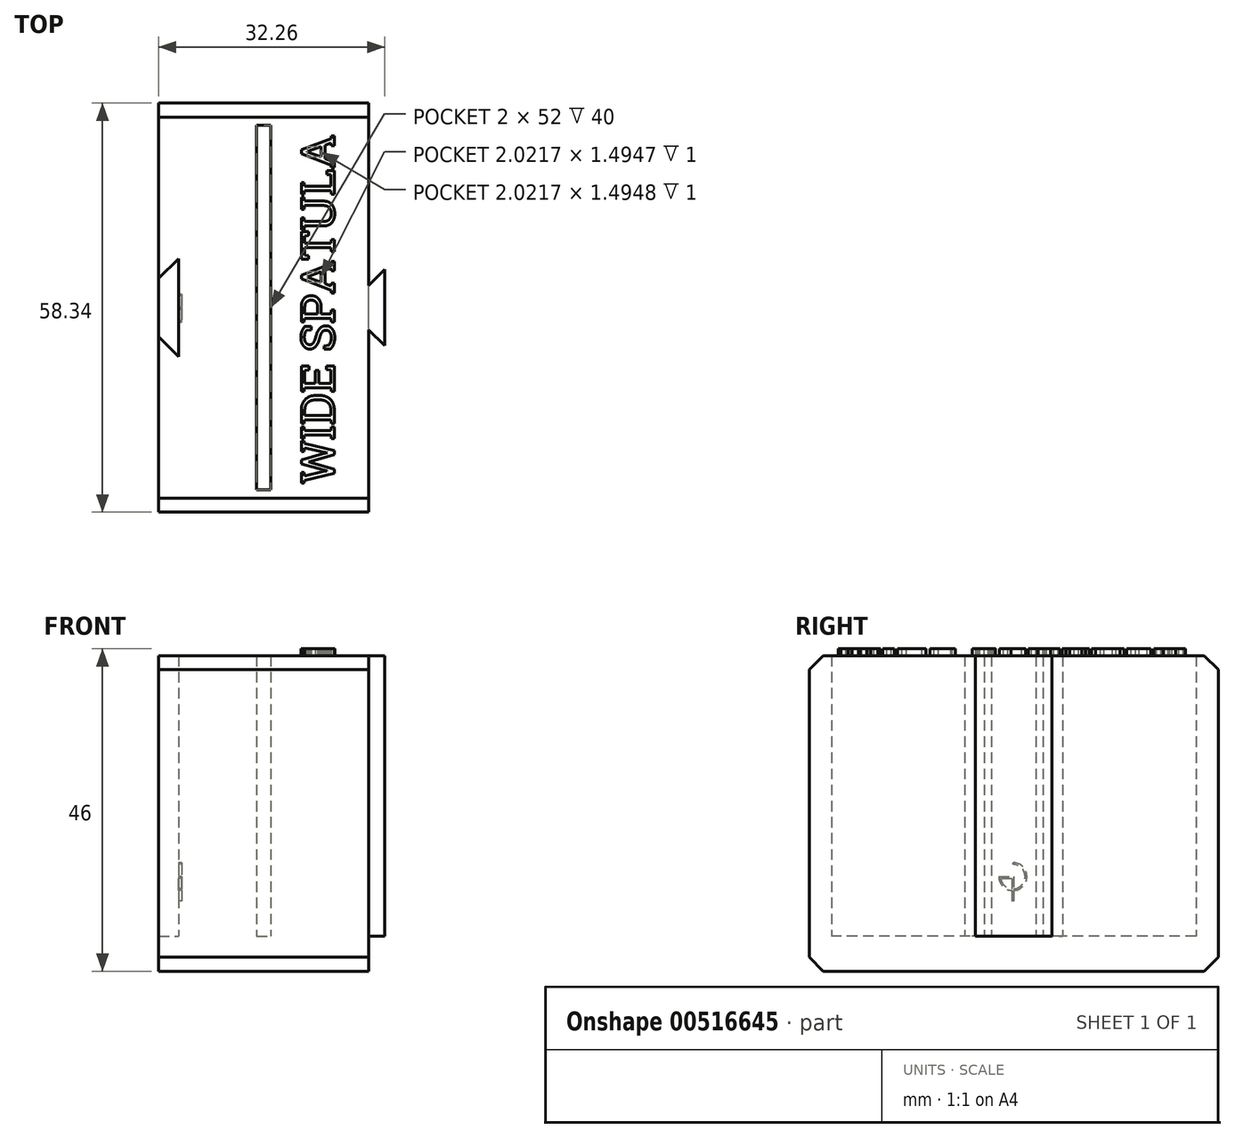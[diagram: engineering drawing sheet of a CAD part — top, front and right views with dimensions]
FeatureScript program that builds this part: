
annotation { "Feature Type Name" : "Feature", "Feature Type Description" : "" }
export const myFeature = defineFeature(function(context is Context, id is Id, definition is map)
    precondition{}
    {
        {
            var Q0;
            Q0=qCreatedBy(makeId("Top.planeOp"),FACE);
            var sketch = newSketch(context, id + "F0", { "sketchPlane" : qUnion([Q0])});
            skLineSegment(sketch, "E0", {"start": v(-15, 4.17) * mm, "end": v(-15, 29.17) * mm});
            skLineSegment(sketch, "E1", {"start": v(-15, 29.17) * mm, "end": v(15, 29.17) * mm});
            skLineSegment(sketch, "E2", {"start": v(15, 29.17) * mm, "end": v(15, 3.17) * mm});
            skLineSegment(sketch, "E3", {"start": v(-15, 4.17) * mm, "end": v(-12.17, 7) * mm});
            skLineSegment(sketch, "E4", {"start": v(-12.17, 7) * mm, "end": v(-12.17, 0) * mm});
            skLineSegment(sketch, "E5", {"start": v(15, 3.17) * mm, "end": v(17.26, 5.43) * mm});
            skLineSegment(sketch, "E6", {"start": v(17.26, 5.43) * mm, "end": v(17.26, -0.57) * mm});
            skLineSegment(sketch, "E7.MirrorCS", {"start": v(-15, -4.17) * mm, "end": v(-12.17, -7) * mm});
            skLineSegment(sketch, "E8.MirrorCS", {"start": v(15, -29.17) * mm, "end": v(15, -3.17) * mm});
            skLineSegment(sketch, "E9.MirrorCS", {"start": v(-12.17, -7) * mm, "end": v(-12.17, 0) * mm});
            skLineSegment(sketch, "E10.MirrorCS", {"start": v(-15, -4.17) * mm, "end": v(-15, -29.17) * mm});
            skLineSegment(sketch, "E11.MirrorCS", {"start": v(17.26, -5.43) * mm, "end": v(17.26, 0.57) * mm});
            skLineSegment(sketch, "E12.MirrorCS", {"start": v(15, -3.17) * mm, "end": v(17.26, -5.43) * mm});
            skLineSegment(sketch, "E13.MirrorCS", {"start": v(-15, -29.17) * mm, "end": v(15, -29.17) * mm});
            skLineSegment(sketch, "E14.bottom", {"start": v(-1, 26) * mm, "end": v(1, 26) * mm});
            skLineSegment(sketch, "E14.top", {"start": v(-1, -26) * mm, "end": v(1, -26) * mm});
            skLineSegment(sketch, "E14.left", {"start": v(-1, 26) * mm, "end": v(-1, -26) * mm});
            skLineSegment(sketch, "E14.right", {"start": v(1, 26) * mm, "end": v(1, -26) * mm});
            skPoint(sketch, "E14.middle", {"position": v(0, 0) * mm});
            skLineSegment(sketch, "E15", {"start": v(-15, 4.17) * mm, "end": v(-15, -4.17) * mm});
            skLineSegment(sketch, "E16", {"start": v(15, 3.17) * mm, "end": v(15, -3.17) * mm});
            skSolve(sketch);
        }
        {
            var Q0;
            Q0=makeQuery(id+"F0.imprint","IMPRINT",FACE,{"disambiguationData":[TD([[makeQuery(id+"F0.imprint","IMPRINT",EDGE,{"derivedFrom":sQuery(id+"F0.wireOp",EDGE,"E5")}),-1.0]])]});
            var Q1;
            Q1=makeQuery(id+"F0.imprint","IMPRINT",FACE,{"disambiguationData":[TD([[makeQuery(id+"F0.imprint","IMPRINT",EDGE,{"derivedFrom":sQuery(id+"F0.wireOp",EDGE,"E0")}),-1.0]])]});
            extrude(context, id + "F1", {"entities" : qUnion([Q0, Q1]), "depth" : 40 * mm, "offsetDistance" : 25 * mm});
        }
        {
            var Q0;
            Q0=makeQuery(id+"F0.imprint","IMPRINT",FACE,{"disambiguationData":[TD([[makeQuery(id+"F0.imprint","IMPRINT",EDGE,{"derivedFrom":sQuery(id+"F0.wireOp",EDGE,"E0")}),-1.0]])]});
            var Q1;
            Q1=makeQuery(id+"F0.imprint","IMPRINT",FACE,{"disambiguationData":[TD([[makeQuery(id+"F0.imprint","IMPRINT",EDGE,{"derivedFrom":sQuery(id+"F0.wireOp",EDGE,"E14.bottom")}),-1.0]])]});
            var Q2;
            Q2=makeQuery(id+"F0.imprint","IMPRINT",FACE,{"disambiguationData":[TD([[makeQuery(id+"F0.imprint","IMPRINT",EDGE,{"derivedFrom":sQuery(id+"F0.wireOp",EDGE,"E3")}),-1.0]])]});
            extrude(context, id + "F2", {"entities" : qUnion([Q0, Q1, Q2]), "operationType" : NewBodyOperationType.ADD, "oppositeDirection" : true, "depth" : 5 * mm, "offsetDistance" : 25 * mm});
        }
        {
            var Q0;
            Q0=makeQuery(id+"F2.opExtrude","CAP_EDGE",EDGE,{"disambiguationData":[OSD([sQuery(id+"F0.wireOp",EDGE,"E13.MirrorCS")])],"isStart":false});
            var Q1;
            Q1=makeQuery(id+"F2.opExtrude","CAP_EDGE",EDGE,{"disambiguationData":[OSD([sQuery(id+"F0.wireOp",EDGE,"E1")])],"isStart":false});
            var Q2;
            Q2=makeQuery(id+"F1.opExtrude","CAP_EDGE",EDGE,{"disambiguationData":[OSD([sQuery(id+"F0.wireOp",EDGE,"E13.MirrorCS")])],"isStart":false});
            var Q3;
            Q3=makeQuery(id+"F1.opExtrude","CAP_EDGE",EDGE,{"disambiguationData":[OSD([sQuery(id+"F0.wireOp",EDGE,"E1")])],"isStart":false});
            chamfer(context, id + "F3", {"entities" : qUnion([Q0, Q1, Q2, Q3]), "width" : 2 * mm, "tangentPropagation" : true});
        }
        {
            var Q0;
            Q0=makeQuery(id+"F1.opExtrude","CAP_FACE",FACE,{"disambiguationData":[OSD([sQuery(id+"F0.wireOp",EDGE,"E0"),sQuery(id+"F0.wireOp",EDGE,"E1"),sQuery(id+"F0.wireOp",EDGE,"E2"),sQuery(id+"F0.wireOp",EDGE,"E3"),sQuery(id+"F0.wireOp",EDGE,"E4"),sQuery(id+"F0.wireOp",EDGE,"E5"),sQuery(id+"F0.wireOp",EDGE,"E6"),sQuery(id+"F0.wireOp",EDGE,"E7.MirrorCS"),sQuery(id+"F0.wireOp",EDGE,"E8.MirrorCS"),sQuery(id+"F0.wireOp",EDGE,"E9.MirrorCS"),sQuery(id+"F0.wireOp",EDGE,"E10.MirrorCS"),sQuery(id+"F0.wireOp",EDGE,"E11.MirrorCS"),sQuery(id+"F0.wireOp",EDGE,"E12.MirrorCS"),sQuery(id+"F0.wireOp",EDGE,"E13.MirrorCS"),sQuery(id+"F0.wireOp",EDGE,"E14.bottom"),sQuery(id+"F0.wireOp",EDGE,"E14.top"),sQuery(id+"F0.wireOp",EDGE,"E14.left"),sQuery(id+"F0.wireOp",EDGE,"E14.right")])],"isStart":false});
            var sketch = newSketch(context, id + "F4", { "sketchPlane" : qUnion([Q0])});
            skText(sketch, "E17", { "text": "WIDE SPATULA", "fontName": "RobotoSlab-Regular.ttf"});
            const initialGuessF4  = {"E17": [0.01007, -0.0251, 0, 1, 0.00477]};
            skSetInitialGuess(sketch, initialGuessF4);
            skSolve(sketch);
        }
        {
            var Q0;
            Q0=qSketchRegion(id+"F4",true);
            extrude(context, id + "F5", {"entities" : qUnion([Q0]), "operationType" : NewBodyOperationType.ADD, "depth" : 1 * mm});
        }
        {
            var Q0;
            Q0=makeQuery(id+"F1.opExtrude","SWEPT_FACE",FACE,{"disambiguationData":[OSD([sQuery(id+"F0.wireOp",EDGE,"E4"),sQuery(id+"F0.wireOp",EDGE,"E9.MirrorCS")])]});
            var sketch = newSketch(context, id + "F6", { "sketchPlane" : qUnion([Q0])});
            skLineSegment(sketch, "E18.bottom", {"start": v(0.12, 10.5) * mm, "end": v(2.12, 10.5) * mm, "construction": true});
            skLineSegment(sketch, "E18.top", {"start": v(0.12, 8.5) * mm, "end": v(2.12, 8.5) * mm, "construction": true});
            skLineSegment(sketch, "E18.left", {"start": v(0.12, 10.5) * mm, "end": v(0.12, 8.5) * mm, "construction": true});
            skLineSegment(sketch, "E18.right", {"start": v(2.12, 10.5) * mm, "end": v(2.12, 8.5) * mm, "construction": true});
            skArc(sketch, "E19", {"start": v(0.12, 10.5) * mm, "mid": v(-1.3, 7.09) * mm, "end": v(2.12, 8.5) * mm});
            skLineSegment(sketch, "E20", {"start": v(0.12, 10.5) * mm, "end": v(0.12, 10.25) * mm});
            skLineSegment(sketch, "E21", {"start": v(2.12, 8.5) * mm, "end": v(1.87, 8.5) * mm});
            skArc(sketch, "E22", {"start": v(0.12, 10.25) * mm, "mid": v(-1.12, 7.26) * mm, "end": v(1.87, 8.5) * mm});
            skLineSegment(sketch, "E23", {"start": v(1.87, 8.5) * mm, "end": v(0, 8.5) * mm});
            skLineSegment(sketch, "E24", {"start": v(0, 8.5) * mm, "end": v(0, 5) * mm});
            skLineSegment(sketch, "E25", {"start": v(0, 5) * mm, "end": v(0.25, 5) * mm});
            skLineSegment(sketch, "E26", {"start": v(1.85, 8.25) * mm, "end": v(0.25, 8.25) * mm});
            skLineSegment(sketch, "E27", {"start": v(0.25, 8.25) * mm, "end": v(0.25, 5) * mm});
            skSolve(sketch);
        }
        {
            var Q0;
            {var subQ0=sQuery(id+"F6.wireOp",EDGE,"E20");Q0=makeQuery(id+"F6.imprint","IMPRINT",FACE,{"disambiguationData":[TD([[makeQuery(id+"F6.imprint","IMPRINT",EDGE,{"derivedFrom":subQ0}),-1.0]])]});}
            var Q1;
            {var subQ1=sQuery(id+"F6.wireOp",EDGE,"E23");Q1=makeQuery(id+"F6.imprint","IMPRINT",FACE,{"disambiguationData":[TD([[makeQuery(id+"F6.imprint","IMPRINT",EDGE,{"derivedFrom":subQ1}),1.0]])]});}
            var Q2;
            {var subQ0=sQuery(id+"F6.wireOp",EDGE,"E24");var subQ1=sQuery(id+"F6.wireOp",EDGE,"E19");var subQ2=makeQuery(id+"F6.imprint","INTERSECT",VERTEX,{"derivedFrom":[subQ1,subQ0]});Q2=makeQuery(id+"F6.imprint","IMPRINT",FACE,{"disambiguationData":[TD([[makeQuery(id+"F6.imprint","IMPRINT",EDGE,{"disambiguationData":[TD([[subQ2,-1.0]])],"derivedFrom":subQ1}),1.0]])]});}
            var Q3;
            {var subQ5=sQuery(id+"F6.wireOp",EDGE,"E25");Q3=makeQuery(id+"F6.imprint","IMPRINT",FACE,{"disambiguationData":[TD([[makeQuery(id+"F6.imprint","IMPRINT",EDGE,{"derivedFrom":subQ5}),1.0]])]});}
            var Q4;
            {var subQ1=sQuery(id+"F6.wireOp",EDGE,"E21");Q4=makeQuery(id+"F6.imprint","IMPRINT",FACE,{"disambiguationData":[TD([[makeQuery(id+"F6.imprint","IMPRINT",EDGE,{"derivedFrom":subQ1}),1.0]])]});}
            extrude(context, id + "F7", {"entities" : qUnion([Q0, Q1, Q2, Q3, Q4]), "operationType" : NewBodyOperationType.REMOVE, "oppositeDirection" : true, "depth" : .5 * mm, "offsetDistance" : 25 * mm});
        }
    });
